# Revit family: T-501_Ciclon FIT1
name_source: partatom
category: Plumbing Fixtures
revit_build: Autodesk Revit 2015 (Build: 20140606_1530(x64)
units: mm (PartAtom-declared; Revit-internal decimal feet)

## types (1)
- T-501_CICLON FIT1
    Altura máx. de bombeo = 5 m vertical
    Carga aparente = 125 VA
    Caudal = 1.7 L/s
    Certificados = http://www.jimten.com
    Clasificación de cargas = Aparato eléctrico - Unidad de vivienda
    Description = TRITURADOR SANITARIO PARA WC
    Diámetro Impulsión = 32 mm  [stored 0.104987 ft]
    Diámetro WC = 100 mm  [stored 0.328084 ft]
    Electricidad = 220-240 VAC 50HZ
    Electrodomésticos = No
    Entradas = WC
    Manufacturer = Jimten
    Material = Polipropileno (Blanco)
    Model = T-501 CICLON FIT1
    Número de polos = 1
    Potencia = 420 W
    Radio Impulsión = 16 mm  [stored 0.0524934 ft]
    Referencia = 75701
    Salida = 1 x Ø32mm
    Type Comments = FACIL MANTENIMIENTO GRACIAS A SU SISTEMA CASET. SILENCIOSO.
    URL = http://www.jimten.com
    Ud.Desagüe = 2
    Voltaje = 230 V
    WC = Yes
    WFU = 2

note: [stored X ft] marks values corroborated as IEEE doubles in the binary element streams (Revit-internal decimal feet)

## geometry (parser evidence)
native form markers: Blend x3, Sweep x3
no freeform markers — native parametric forms only
